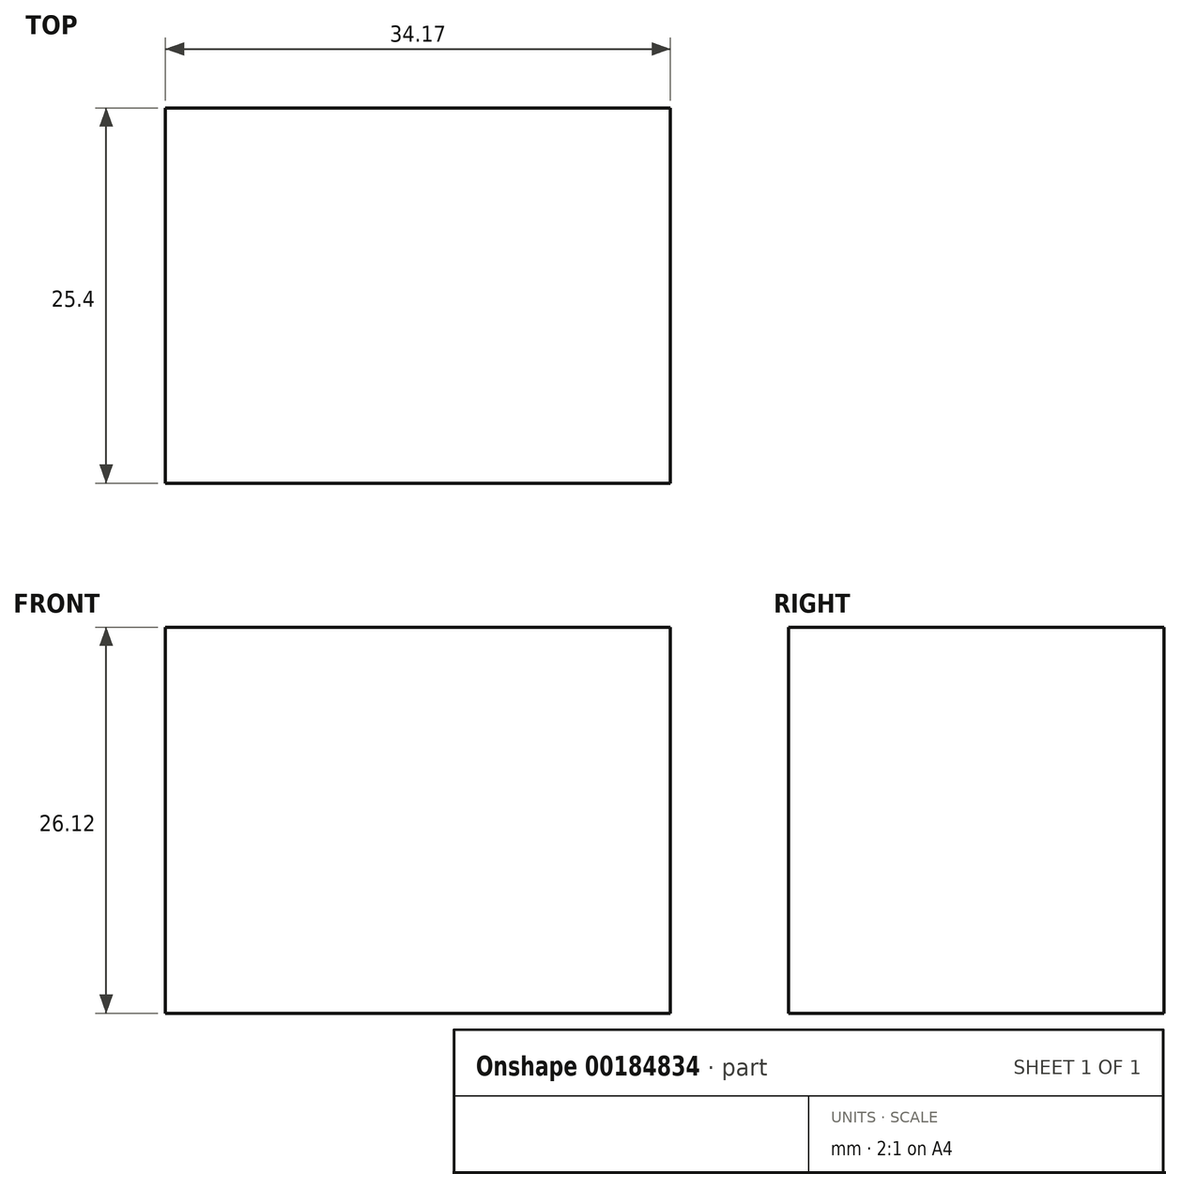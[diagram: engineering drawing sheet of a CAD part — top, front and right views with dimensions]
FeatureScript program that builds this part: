
annotation { "Feature Type Name" : "Feature", "Feature Type Description" : "" }
export const myFeature = defineFeature(function(context is Context, id is Id, definition is map)
    precondition{}
    {
        {
            var Q0;
            Q0=qCreatedBy(makeId("Front.planeOp"),FACE);
            var sketch = newSketch(context, id + "F0", { "sketchPlane" : qUnion([Q0])});
            skLineSegment(sketch, "E0.bottom", {"start": v(-13.14, 14.13) * mm, "end": v(21.03, 14.13) * mm});
            skLineSegment(sketch, "E0.top", {"start": v(-13.14, -12) * mm, "end": v(21.03, -12) * mm});
            skLineSegment(sketch, "E0.left", {"start": v(-13.14, 14.13) * mm, "end": v(-13.14, -12) * mm});
            skLineSegment(sketch, "E0.right", {"start": v(21.03, 14.13) * mm, "end": v(21.03, -12) * mm});
            skSolve(sketch);
        }
        {
            var Q0;
            Q0 = qSketchRegion(id + "F0", true);
            extrude(context, id + "F1", {"entities" : qUnion([Q0]), "oppositeDirection" : true, "depth" : 25.4 * mm});
        }
    });
